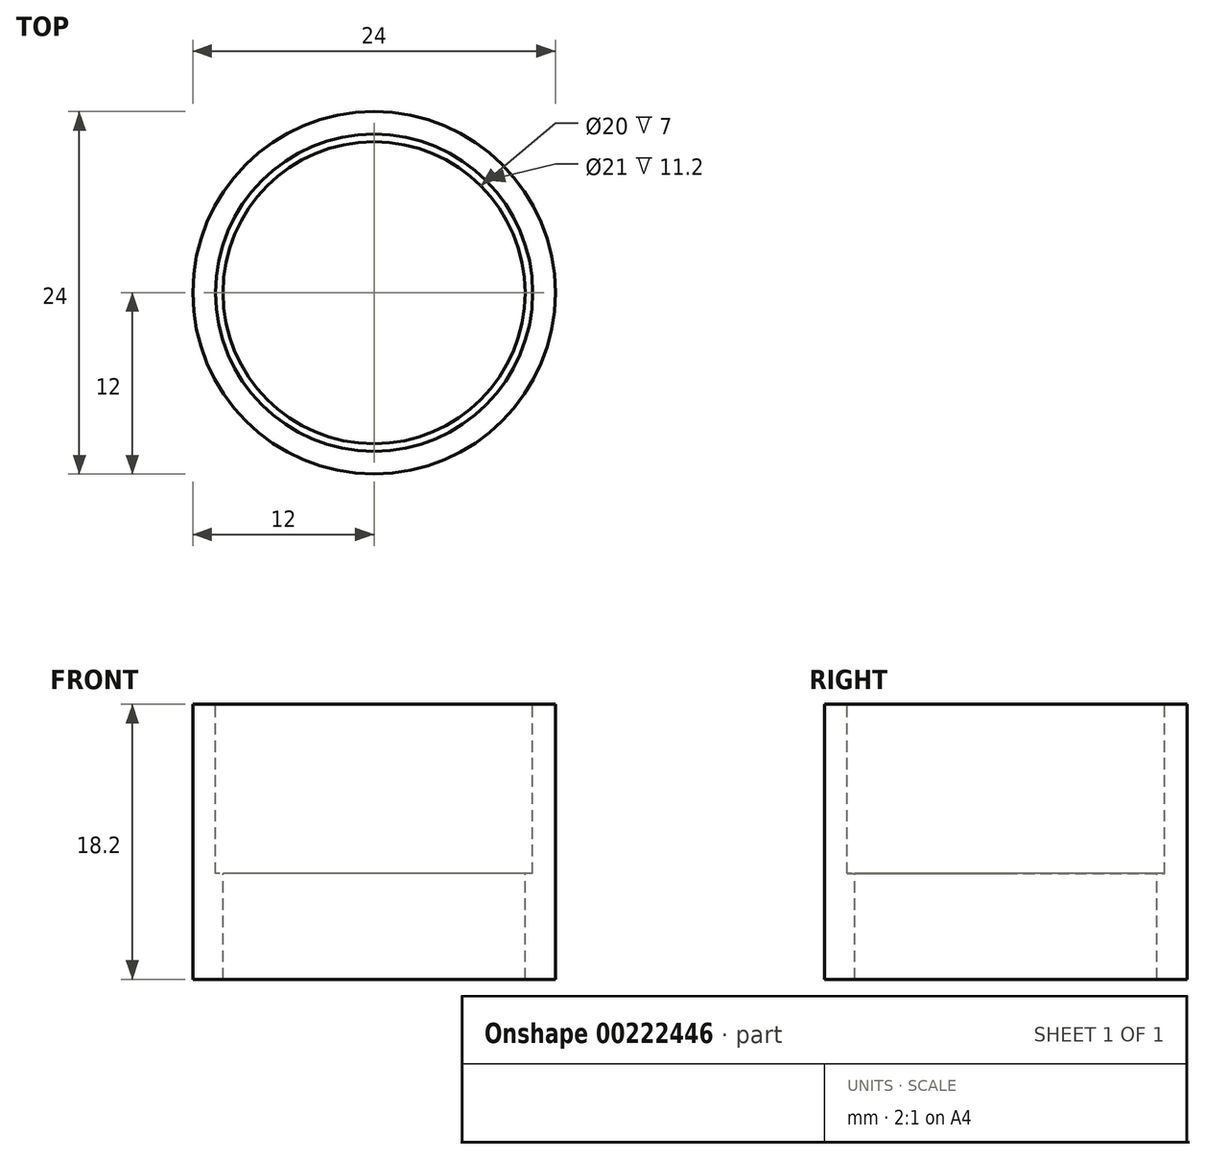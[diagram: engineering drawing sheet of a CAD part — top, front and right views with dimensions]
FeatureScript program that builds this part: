
annotation { "Feature Type Name" : "Feature", "Feature Type Description" : "" }
export const myFeature = defineFeature(function(context is Context, id is Id, definition is map)
    precondition{}
    {
        {
            var Q0;
            Q0=qCreatedBy(makeId("Front.planeOp"),FACE);
            var sketch = newSketch(context, id + "F0", { "sketchPlane" : qUnion([Q0])});
            skLineSegment(sketch, "E0", {"start": v(0, 6.94) * mm, "end": v(0, -7.35) * mm, "construction": true});
            skLineSegment(sketch, "E1", {"start": v(-10, 0) * mm, "end": v(-12, 0) * mm});
            skLineSegment(sketch, "E2", {"start": v(-12, 0) * mm, "end": v(-12, 18.2) * mm});
            skLineSegment(sketch, "E3", {"start": v(-12, 18.2) * mm, "end": v(-10.5, 18.2) * mm});
            skLineSegment(sketch, "E4", {"start": v(-10.5, 18.2) * mm, "end": v(-10.5, 7) * mm});
            skLineSegment(sketch, "E5", {"start": v(-10.5, 7) * mm, "end": v(-10, 7) * mm});
            skLineSegment(sketch, "E6", {"start": v(-10, 7) * mm, "end": v(-10, 0) * mm});
            skSolve(sketch);
        }
        {
            var Q0;
            Q0 = qSketchRegion(id + "F0", true);
            var Q1;
            Q1=sQuery(id+"F0.wireOp",EDGE,"E0");
            revolve(context, id + "F1", {"entities" : qUnion([Q0]), "axis" : qUnion([Q1]), "revolveType" : RevolveType.FULL});
        }
    });
